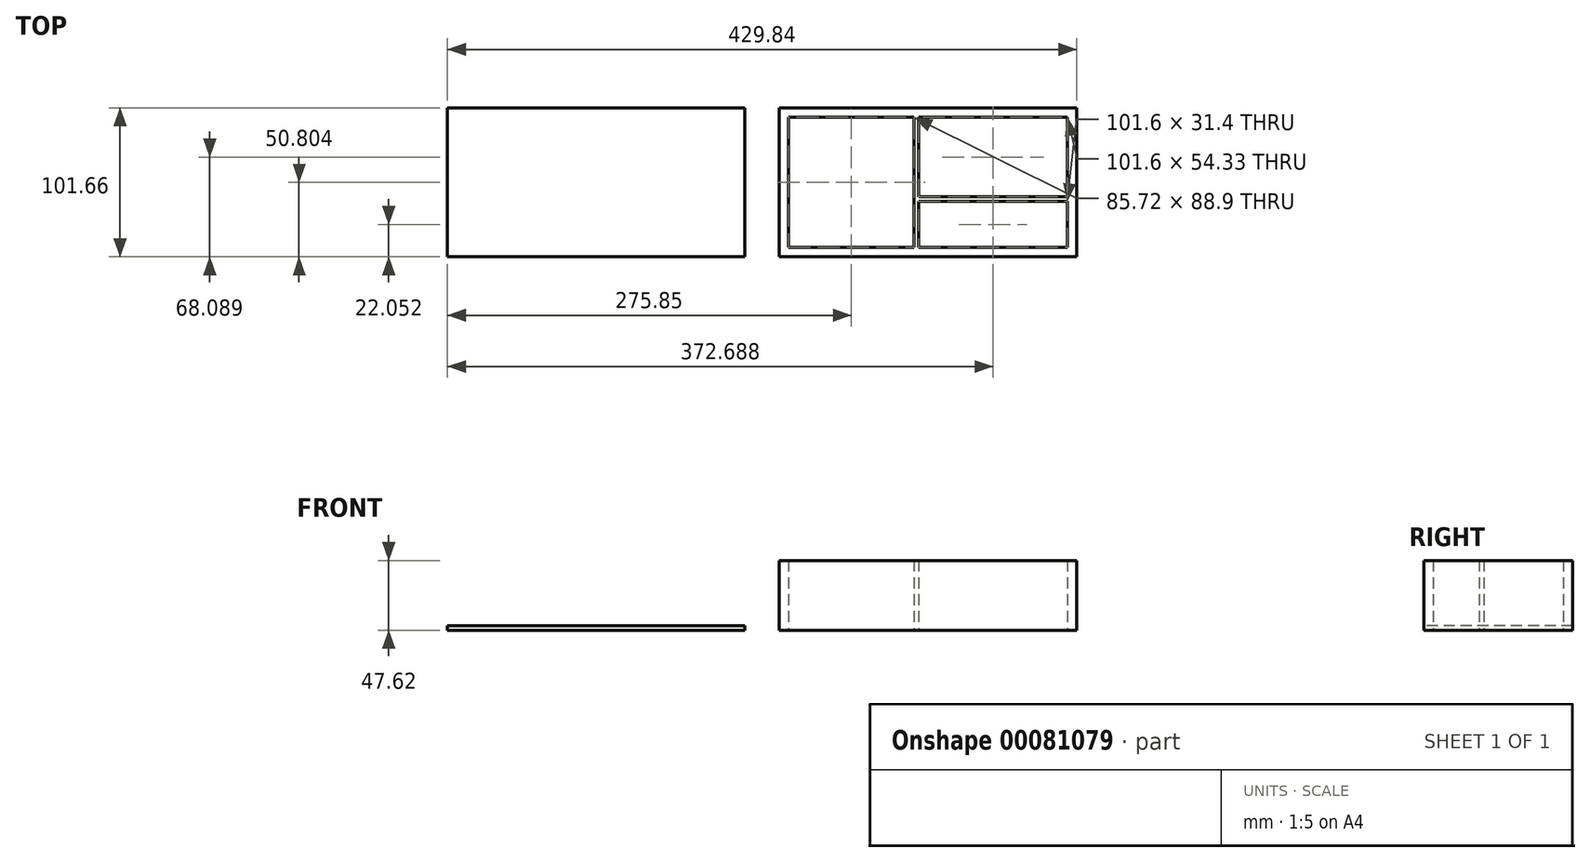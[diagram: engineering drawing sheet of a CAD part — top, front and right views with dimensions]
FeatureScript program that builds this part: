
annotation { "Feature Type Name" : "Feature", "Feature Type Description" : "" }
export const myFeature = defineFeature(function(context is Context, id is Id, definition is map)
    precondition{}
    {
        {
            var Q0;
            Q0=qCreatedBy(makeId("Top.planeOp"),FACE);
            var sketch = newSketch(context, id + "F0", { "sketchPlane" : qUnion([Q0])});
            skLineSegment(sketch, "E0.bottom", {"start": v(-56.23, 54.28) * mm, "end": v(146.97, 54.28) * mm});
            skLineSegment(sketch, "E0.top", {"start": v(-56.23, -47.32) * mm, "end": v(146.97, -47.32) * mm});
            skLineSegment(sketch, "E0.left", {"start": v(-56.23, 54.28) * mm, "end": v(-56.23, -47.32) * mm});
            skLineSegment(sketch, "E0.right", {"start": v(146.97, 54.28) * mm, "end": v(146.97, -47.32) * mm});
            skLineSegment(sketch, "E1.bottom", {"start": v(-282.87, 54.34) * mm, "end": v(-79.67, 54.34) * mm});
            skLineSegment(sketch, "E1.top", {"start": v(-282.87, -47.26) * mm, "end": v(-79.67, -47.26) * mm});
            skLineSegment(sketch, "E1.left", {"start": v(-282.87, 54.34) * mm, "end": v(-282.87, -47.26) * mm});
            skLineSegment(sketch, "E1.right", {"start": v(-79.67, 54.34) * mm, "end": v(-79.67, -47.26) * mm});
            skLineSegment(sketch, "E2.bottom", {"start": v(-49.88, 47.93) * mm, "end": v(35.84, 47.93) * mm});
            skLineSegment(sketch, "E2.top", {"start": v(-49.88, -40.97) * mm, "end": v(35.84, -40.97) * mm});
            skLineSegment(sketch, "E2.left", {"start": v(-49.88, 47.93) * mm, "end": v(-49.88, -40.97) * mm});
            skLineSegment(sketch, "E2.right", {"start": v(35.84, 47.93) * mm, "end": v(35.84, -40.97) * mm});
            skLineSegment(sketch, "E3.bottom", {"start": v(39.02, 47.93) * mm, "end": v(140.62, 47.93) * mm});
            skLineSegment(sketch, "E3.top", {"start": v(39.02, -6.4) * mm, "end": v(140.62, -6.4) * mm});
            skLineSegment(sketch, "E3.left", {"start": v(39.02, 47.93) * mm, "end": v(39.02, -6.4) * mm});
            skLineSegment(sketch, "E3.right", {"start": v(140.62, 47.93) * mm, "end": v(140.62, -6.4) * mm});
            skLineSegment(sketch, "E4.bottom", {"start": v(39.02, -9.57) * mm, "end": v(140.62, -9.57) * mm});
            skLineSegment(sketch, "E4.top", {"start": v(39.02, -40.97) * mm, "end": v(140.62, -40.97) * mm});
            skLineSegment(sketch, "E4.left", {"start": v(39.02, -9.57) * mm, "end": v(39.02, -40.97) * mm});
            skLineSegment(sketch, "E4.right", {"start": v(140.62, -9.57) * mm, "end": v(140.62, -40.97) * mm});
            skSolve(sketch);
        }
        {
            var Q0;
            Q0=makeQuery(id+"F0.imprint","IMPRINT",FACE,{"disambiguationData":[TD([[makeQuery(id+"F0.imprint","IMPRINT",EDGE,{"derivedFrom":sQuery(id+"F0.wireOp",EDGE,"E1.bottom")}),-1.0]])]});
            extrude(context, id + "F1", {"entities" : qUnion([Q0]), "depth" : 3.17 * mm});
        }
        {
            var Q0;
            Q0=makeQuery(id+"F0.imprint","IMPRINT",FACE,{"disambiguationData":[TD([[makeQuery(id+"F0.imprint","IMPRINT",EDGE,{"derivedFrom":sQuery(id+"F0.wireOp",EDGE,"E0.bottom")}),-1.0]])]});
            extrude(context, id + "F2", {"entities" : qUnion([Q0]), "depth" : 47.62 * mm});
        }
    });
